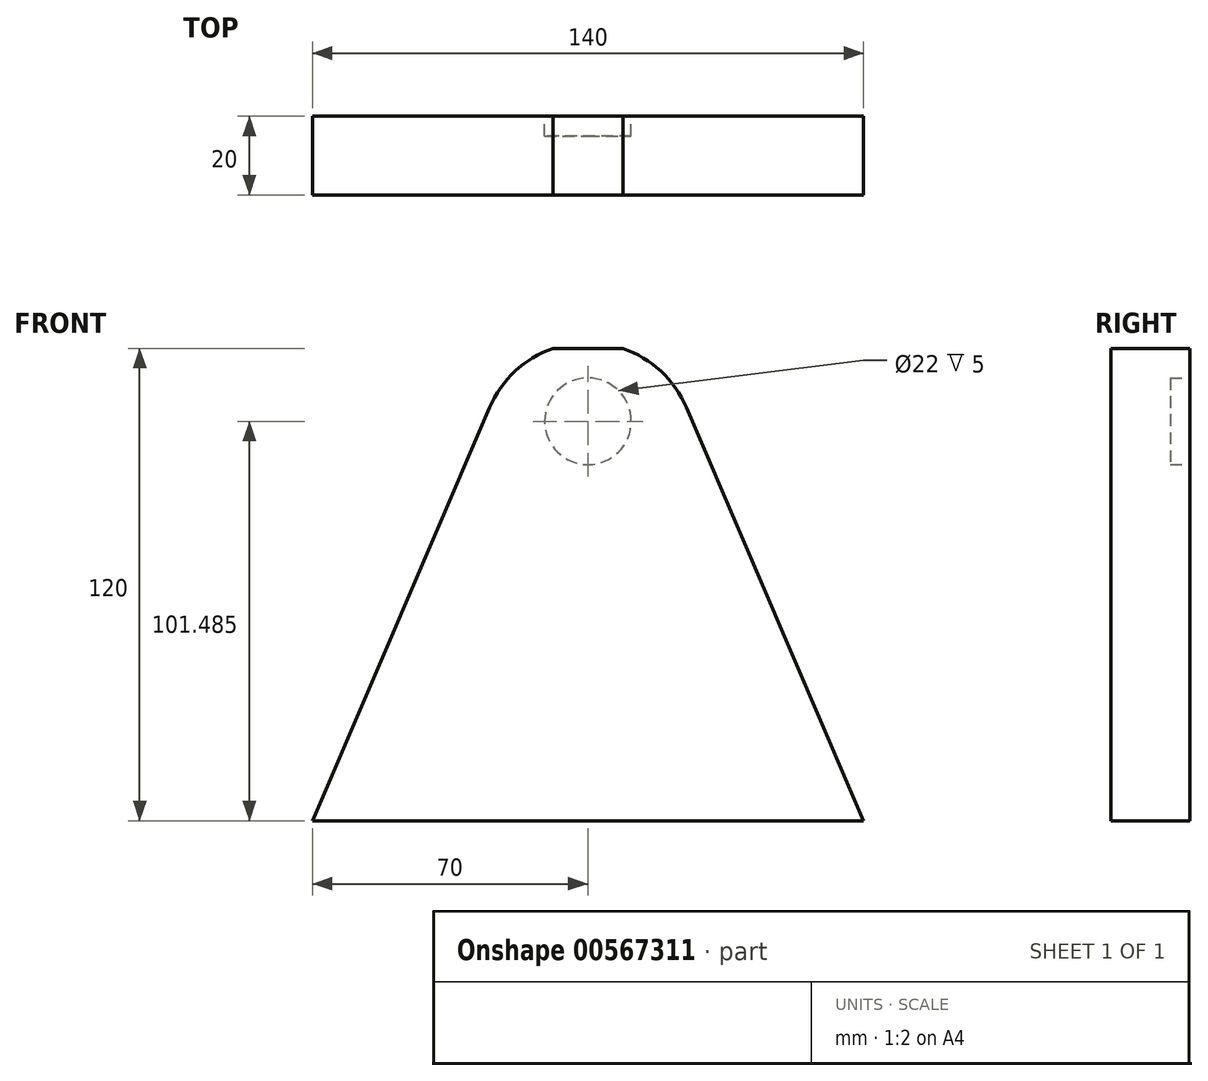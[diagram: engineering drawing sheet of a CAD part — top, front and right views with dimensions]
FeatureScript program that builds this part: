
annotation { "Feature Type Name" : "Feature", "Feature Type Description" : "" }
export const myFeature = defineFeature(function(context is Context, id is Id, definition is map)
    precondition{}
    {
        {
            var Q0;
            Q0=qCreatedBy(makeId("Front.planeOp"),FACE);
            var sketch = newSketch(context, id + "F0", { "sketchPlane" : qUnion([Q0])});
            skLineSegment(sketch, "E0.bottom", {"start": v(70, 70) * mm, "end": v(-70, 70) * mm});
            skLineSegment(sketch, "E0.top", {"start": v(70, -70) * mm, "end": v(-70, -70) * mm});
            skLineSegment(sketch, "E0.left", {"start": v(70, 70) * mm, "end": v(70, -70) * mm});
            skLineSegment(sketch, "E0.right", {"start": v(-70, 70) * mm, "end": v(-70, -70) * mm});
            skPoint(sketch, "E0.middle", {"position": v(0, 0) * mm});
            skLineSegment(sketch, "E1.bottom", {"start": v(-70, -70) * mm, "end": v(70, -70) * mm});
            skLineSegment(sketch, "E1.top", {"start": v(-70, -50) * mm, "end": v(70, -50) * mm});
            skLineSegment(sketch, "E1.left", {"start": v(-70, -70) * mm, "end": v(-70, -50) * mm});
            skLineSegment(sketch, "E1.right", {"start": v(70, -70) * mm, "end": v(70, -50) * mm});
            skLineSegment(sketch, "E2", {"start": v(-70, 70) * mm, "end": v(-25, 70) * mm});
            skLineSegment(sketch, "E3", {"start": v(70, 70) * mm, "end": v(25, 70) * mm});
            skLineSegment(sketch, "E4", {"start": v(-25, 70) * mm, "end": v(25, 70) * mm});
            skLineSegment(sketch, "E5", {"start": v(-70, -50) * mm, "end": v(-25, 55) * mm});
            skLineSegment(sketch, "E6", {"start": v(70, -50) * mm, "end": v(25, 55) * mm});
            skArc(sketch, "E7", {"start": v(25, 55) * mm, "mid": v(0, 71.48) * mm, "end": v(-25, 55) * mm});
            skSolve(sketch);
        }
        {
            var Q0;
            Q0=makeQuery(id+"F0.imprint","IMPRINT",FACE,{"disambiguationData":[TD([[makeQuery(id+"F0.imprint","IMPRINT",EDGE,{"derivedFrom":sQuery(id+"F0.wireOp",EDGE,"E1.bottom")}),1.0]])]});
            var Q1;
            {var subQ0=sQuery(id+"F0.wireOp",EDGE,"E7");var subQ1=sQuery(id+"F0.wireOp",EDGE,"E4");var subQ2=makeQuery(id+"F0.imprint","INTERSECT",VERTEX,{"disambiguationData":[OD(0.0)],"derivedFrom":[subQ1,subQ0]});Q1=makeQuery(id+"F0.imprint","IMPRINT",FACE,{"disambiguationData":[TD([[makeQuery(id+"F0.imprint","IMPRINT",EDGE,{"disambiguationData":[TD([[subQ2,-1.0]])],"derivedFrom":subQ1}),1.0]])]});}
            var Q2;
            Q2=makeQuery(id+"F0.imprint","IMPRINT",FACE,{"disambiguationData":[TD([[makeQuery(id+"F0.imprint","IMPRINT",EDGE,{"derivedFrom":sQuery(id+"F0.wireOp",EDGE,"E1.top")}),1.0]])]});
            extrude(context, id + "F1", {"entities" : qUnion([Q0, Q1, Q2]), "depth" : 20 * mm, "offsetDistance" : 25 * mm});
        }
        {
            var Q0;
            Q0=makeQuery(id+"F1.opExtrude","CAP_FACE",FACE,{"disambiguationData":[OSD([sQuery(id+"F0.wireOp",EDGE,"E1.bottom"),sQuery(id+"F0.wireOp",EDGE,"E1.left"),sQuery(id+"F0.wireOp",EDGE,"E1.right"),sQuery(id+"F0.wireOp",EDGE,"E5"),sQuery(id+"F0.wireOp",EDGE,"E6"),sQuery(id+"F0.wireOp",EDGE,"E7")])],"isStart":true});
            var sketch = newSketch(context, id + "F2", { "sketchPlane" : qUnion([Q0])});
            skLineSegment(sketch, "E8", {"start": v(0, 71.48) * mm, "end": v(0, 51.48) * mm});
            skPoint(sketch, "E8.endSnap0", {"position": v(0, 71.48) * mm});
            skCircle(sketch, "E9", {"center": v(0, 51.48) * mm, "radius": 11 * mm});
            skSolve(sketch);
        }
        {
            var Q0;
            Q0=makeQuery(id+"F2.imprint","IMPRINT",FACE,{"disambiguationData":[TD([[makeQuery(id+"F2.imprint","IMPRINT",EDGE,{"derivedFrom":sQuery(id+"F2.wireOp",EDGE,"E9")}),1.0]])]});
            extrude(context, id + "F3", {"entities" : qUnion([Q0]), "operationType" : NewBodyOperationType.REMOVE, "oppositeDirection" : true, "depth" : 5 * mm, "offsetDistance" : 25 * mm});
        }
    });
